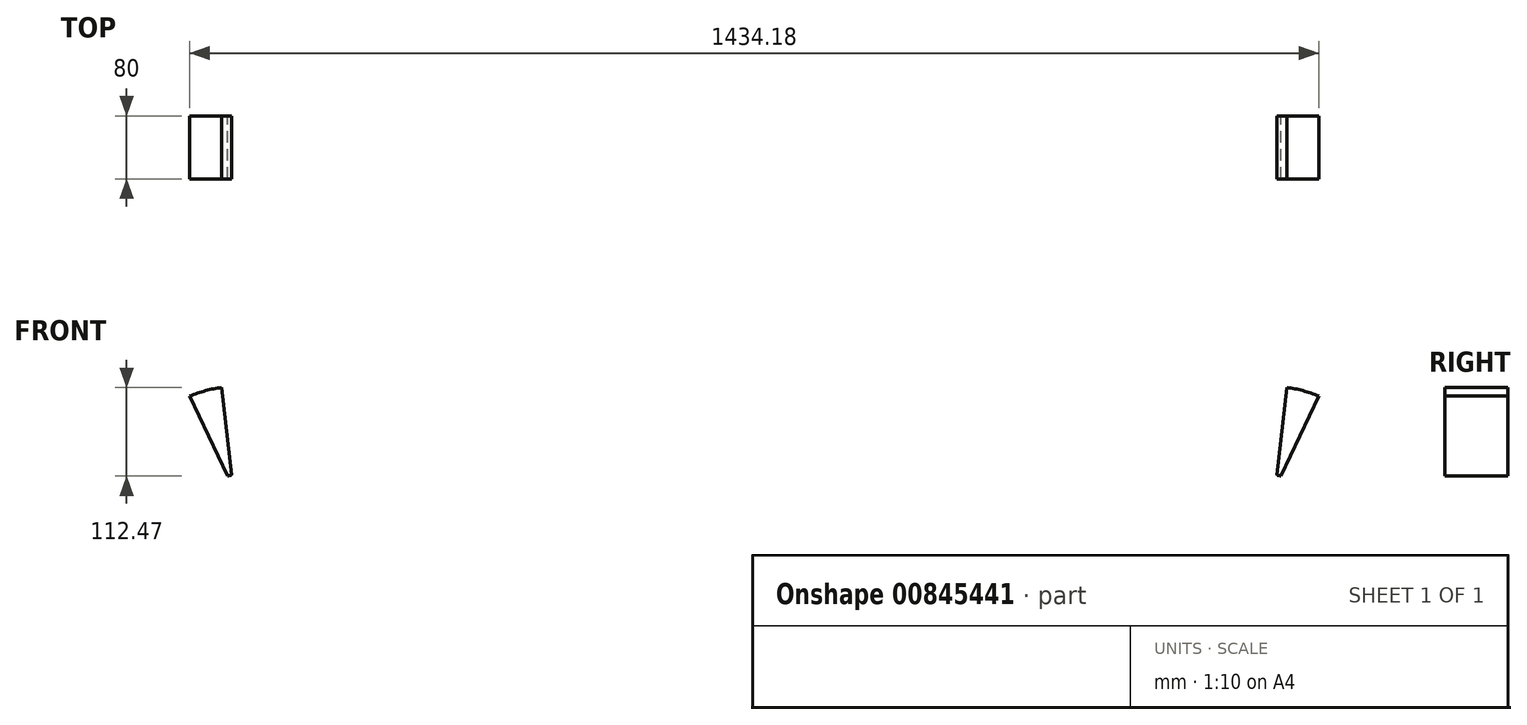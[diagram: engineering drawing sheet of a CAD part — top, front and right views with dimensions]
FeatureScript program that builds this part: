
annotation { "Feature Type Name" : "Feature", "Feature Type Description" : "" }
export const myFeature = defineFeature(function(context is Context, id is Id, definition is map)
    precondition{}
    {
        {
            var Q0;
            Q0=qCreatedBy(makeId("Front.planeOp"),FACE);
            var sketch = newSketch(context, id + "F0", { "sketchPlane" : qUnion([Q0])});
            skCircle(sketch, "E0", {"center": v(-657.5, 0) * mm, "radius": 152 * mm});
            skCircle(sketch, "E1.0", {"center": v(-657.5, 0) * mm, "radius": 162 * mm});
            skCircle(sketch, "E2", {"center": v(-657.5, 0) * mm, "radius": 40 * mm});
            skCircle(sketch, "E3", {"center": v(-657.5, 0) * mm, "radius": 15 * mm});
            skLineSegment(sketch, "E4", {"start": v(-668.9, 38.34) * mm, "end": v(-717.09, 139.83) * mm});
            skLineSegment(sketch, "E5", {"start": v(-664, 39.47) * mm, "end": v(-676.5, 150.8) * mm});
            skSolve(sketch);
        }
        {
            var Q0;
            Q0=makeQuery(id+"FRvkTirpPdmJJv8_0.1.F0.imprint","IMPRINT",FACE,{"disambiguationData":[TD([[makeQuery(id+"FRvkTirpPdmJJv8_0.1.F0.imprint","IMPRINT",EDGE,{"derivedFrom":sQuery(id+"FRvkTirpPdmJJv8_0.1.F0.wireOp",EDGE,"E1.0")}),1.0]])]});
            var Q1;
            {var subQ0=sQuery(id+"FRvkTirpPdmJJv8_0.4.F0.wireOp",EDGE,"E4");Q1=makeQuery(id+"FRvkTirpPdmJJv8_0.4.F0.imprint","IMPRINT",FACE,{"disambiguationData":[TD([[makeQuery(id+"FRvkTirpPdmJJv8_0.4.F0.imprint","IMPRINT",EDGE,{"derivedFrom":subQ0}),-1.0]])]});}
            var Q2;
            {var subQ0=sQuery(id+"FRvkTirpPdmJJv8_0.3.F0.wireOp",EDGE,"E4");Q2=makeQuery(id+"FRvkTirpPdmJJv8_0.3.F0.imprint","IMPRINT",FACE,{"disambiguationData":[TD([[makeQuery(id+"FRvkTirpPdmJJv8_0.3.F0.imprint","IMPRINT",EDGE,{"derivedFrom":subQ0}),-1.0]])]});}
            var Q3;
            {var subQ0=sQuery(id+"FRvkTirpPdmJJv8_0.2.F0.wireOp",EDGE,"E4");Q3=makeQuery(id+"FRvkTirpPdmJJv8_0.2.F0.imprint","IMPRINT",FACE,{"disambiguationData":[TD([[makeQuery(id+"FRvkTirpPdmJJv8_0.2.F0.imprint","IMPRINT",EDGE,{"derivedFrom":subQ0}),-1.0]])]});}
            var Q4;
            {var subQ0=sQuery(id+"F0.wireOp",EDGE,"E4");Q4=makeQuery(id+"F0.imprint","IMPRINT",FACE,{"disambiguationData":[TD([[makeQuery(id+"F0.imprint","IMPRINT",EDGE,{"derivedFrom":subQ0}),-1.0]])]});}
            var Q5;
            {var subQ0=sQuery(id+"FRvkTirpPdmJJv8_0.1.F0.wireOp",EDGE,"E4");Q5=makeQuery(id+"FRvkTirpPdmJJv8_0.1.F0.imprint","IMPRINT",FACE,{"disambiguationData":[TD([[makeQuery(id+"FRvkTirpPdmJJv8_0.1.F0.imprint","IMPRINT",EDGE,{"derivedFrom":subQ0}),-1.0]])]});}
            var Q6;
            Q6=makeQuery(id+"FRvkTirpPdmJJv8_0.4.F0.imprint","IMPRINT",FACE,{"disambiguationData":[TD([[makeQuery(id+"FRvkTirpPdmJJv8_0.4.F0.imprint","IMPRINT",EDGE,{"derivedFrom":sQuery(id+"FRvkTirpPdmJJv8_0.4.F0.wireOp",EDGE,"E3")}),-1.0]])]});
            extrude(context, id + "F1", {"entities" : qUnion([Q0, Q1, Q2, Q3, Q4, Q5, Q6]), "depth" : 80 * mm, "offsetDistance" : 25 * mm, "symmetric" : true});
        }
        {
            var Q0;
            Q0=makeQuery(id+"F1.opExtrude","SWEPT_BODY",BODY,{"disambiguationData":[OSD([sQuery(id+"F0.wireOp",EDGE,"E0"),sQuery(id+"F0.wireOp",EDGE,"E2"),sQuery(id+"F0.wireOp",EDGE,"E4"),sQuery(id+"F0.wireOp",EDGE,"E5")])]});
            var Q1;
            Q1=qCreatedBy(makeId("Right.planeOp"),FACE);
            mirror(context, id + "F2", {"entities" : qUnion([Q0]), "mirrorPlane" : qUnion([Q1])});
        }
    });
